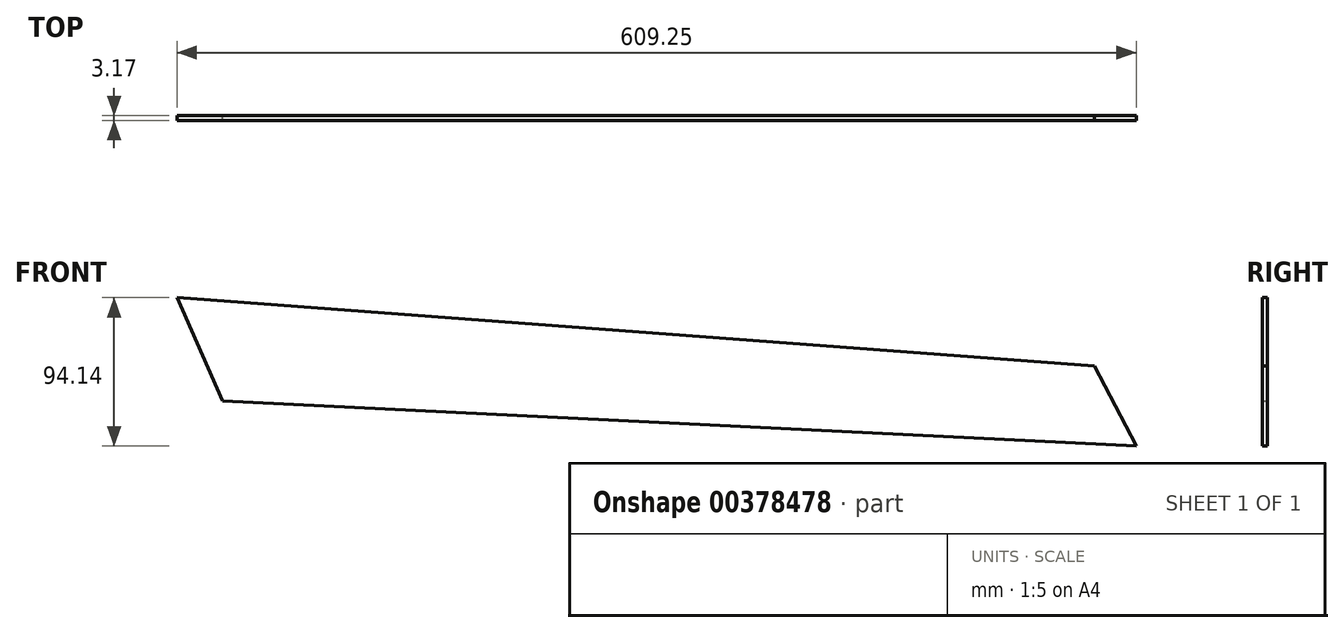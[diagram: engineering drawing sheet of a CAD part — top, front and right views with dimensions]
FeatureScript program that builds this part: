
annotation { "Feature Type Name" : "Feature", "Feature Type Description" : "" }
export const myFeature = defineFeature(function(context is Context, id is Id, definition is map)
    precondition{}
    {
        {
            var Q0;
            Q0=qCreatedBy(makeId("Front.planeOp"),FACE);
            var sketch = newSketch(context, id + "F0", { "sketchPlane" : qUnion([Q0])});
            skLineSegment(sketch, "E0", {"start": v(0, 0) * mm, "end": v(-580.19, 28.67) * mm});
            skLineSegment(sketch, "E1", {"start": v(-580.19, 28.67) * mm, "end": v(-609.25, 94.14) * mm});
            skLineSegment(sketch, "E2", {"start": v(-609.25, 94.14) * mm, "end": v(-26.66, 50.84) * mm});
            skLineSegment(sketch, "E3", {"start": v(-26.66, 50.84) * mm, "end": v(0, 0) * mm});
            skSolve(sketch);
        }
        {
            var Q0;
            Q0 = qSketchRegion(id + "F0", true);
            extrude(context, id + "F1", {"entities" : qUnion([Q0]), "depth" : 3.17 * mm});
        }
    });
